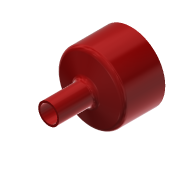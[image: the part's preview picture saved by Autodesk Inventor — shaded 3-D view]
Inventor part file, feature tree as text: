
AUTODESK INVENTOR PART (.ipt)
format: ipt  version: 2019.4 (Build 234330000, 330)  size: 174,592 bytes
history: native  units: mm
features: other x4, sketch x3, reference x3, extrude x2, revolve x1, fillet x1, projected_geometry x1
ambient origin geometry x8: Origin, YZ Plane, XZ Plane, XY Plane, X Axis, Y Axis, Z Axis, Center Point
bodies: Solid1 (feature_tree)
feature tree (15):
  revolve  "Revolution1"  [1 undecoded]
  extrude  "Extrusion2"  Depth=13.0mm
  extrude  "Extrusion3"  Depth=2.0mm
  fillet  "Fillet2"  Radius=5.0mm
  sketch  "Sketch1"  dims[d6=90.0deg d12=4.0mm]
  reference  "Reference1"
  sketch  "Sketch4"  dims[d13=0.0mm d15=13.0mm]
  reference  "Reference2"
  projected_geometry  "Projected Loop2"
  sketch  "Sketch5"  dims[d16=0.0mm d17=2.0mm d19=5.0mm d20=14.0mm d21=6.5mm d22=15.0mm d23=0.0mm d24=2.0mm d25=0.2mm d26=12.0mm d27=-0.523599mm]
  reference  "Reference3"
  other  "Assemlby_OpenOxygen.iam"
  other  "00_Sensirion_Flowsensor:1"
  other  "01_Connector_T:1"
  other  "03_OpenOxygen_Box:1"
note: 1 required parameter value undecoded (feature->parameter linkage not recoverable at this tier; creation-order binding heuristic only, values carry confidence <= 0.55)
